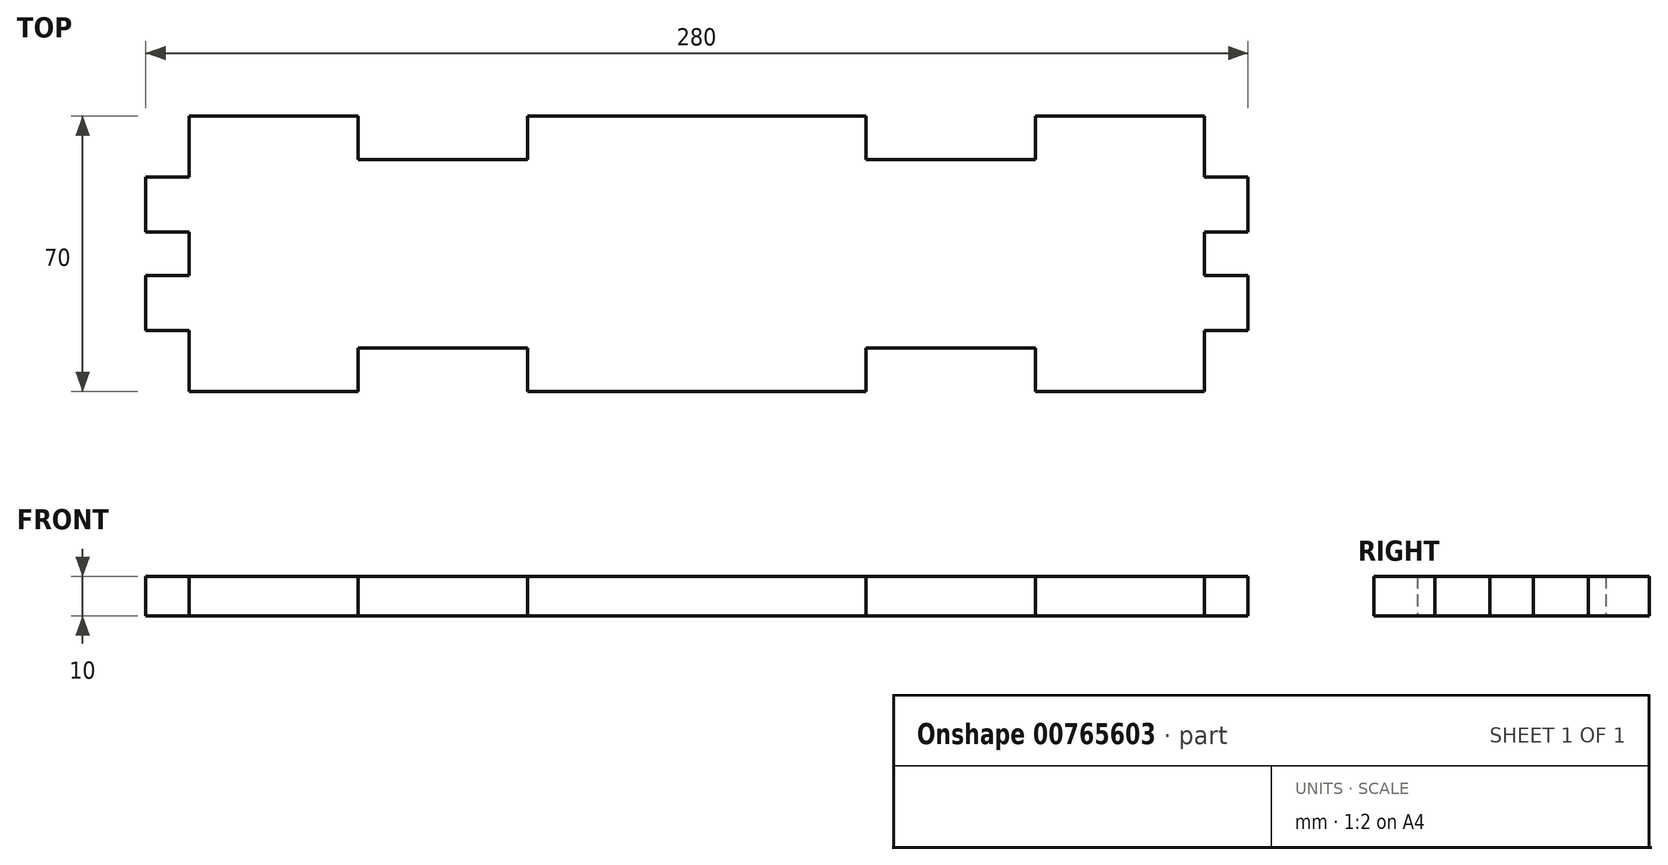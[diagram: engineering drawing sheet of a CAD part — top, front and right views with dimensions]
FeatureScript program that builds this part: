
annotation { "Feature Type Name" : "Feature", "Feature Type Description" : "" }
export const myFeature = defineFeature(function(context is Context, id is Id, definition is map)
    precondition{}
    {
        {
            var Q0;
            Q0=qCreatedBy(makeId("Top.planeOp"),FACE);
            var sketch = newSketch(context, id + "F0", { "sketchPlane" : qUnion([Q0])});
            skPoint(sketch, "E0.middle", {"position": v(0, 0) * mm});
            skLineSegment(sketch, "E1", {"start": v(129, 35) * mm, "end": v(129, 19.5) * mm});
            skLineSegment(sketch, "E2", {"start": v(129, 19.5) * mm, "end": v(140, 19.5) * mm});
            skLineSegment(sketch, "E3", {"start": v(140, 19.5) * mm, "end": v(140, 5.5) * mm});
            skLineSegment(sketch, "E4.MirrorCS", {"start": v(129, -35) * mm, "end": v(129, -19.5) * mm});
            skLineSegment(sketch, "E5.MirrorCS", {"start": v(129, -19.5) * mm, "end": v(140, -19.5) * mm});
            skLineSegment(sketch, "E6.MirrorCS", {"start": v(140, -19.5) * mm, "end": v(140, -5.5) * mm});
            skLineSegment(sketch, "E7", {"start": v(140, -5.5) * mm, "end": v(129, -5.5) * mm});
            skLineSegment(sketch, "E8", {"start": v(129, -5.5) * mm, "end": v(129, 5.5) * mm});
            skLineSegment(sketch, "E9", {"start": v(129, 5.5) * mm, "end": v(140, 5.5) * mm});
            skLineSegment(sketch, "E10.MirrorCS", {"start": v(-129, 35) * mm, "end": v(-129, 19.5) * mm});
            skLineSegment(sketch, "E11.MirrorCS", {"start": v(-129, 19.5) * mm, "end": v(-140, 19.5) * mm});
            skLineSegment(sketch, "E12.MirrorCS", {"start": v(-140, 19.5) * mm, "end": v(-140, 5.5) * mm});
            skLineSegment(sketch, "E13.MirrorCS", {"start": v(-129, 5.5) * mm, "end": v(-140, 5.5) * mm});
            skLineSegment(sketch, "E14.MirrorCS", {"start": v(-129, -5.5) * mm, "end": v(-129, 5.5) * mm});
            skLineSegment(sketch, "E15.MirrorCS", {"start": v(-140, -5.5) * mm, "end": v(-129, -5.5) * mm});
            skLineSegment(sketch, "E16.MirrorCS", {"start": v(-140, -19.5) * mm, "end": v(-140, -5.5) * mm});
            skLineSegment(sketch, "E17.MirrorCS", {"start": v(-129, -19.5) * mm, "end": v(-140, -19.5) * mm});
            skLineSegment(sketch, "E18.MirrorCS", {"start": v(-129, -35) * mm, "end": v(-129, -19.5) * mm});
            skLineSegment(sketch, "E19", {"start": v(-129, 35) * mm, "end": v(-86, 35) * mm});
            skLineSegment(sketch, "E20", {"start": v(-86, 35) * mm, "end": v(-86, 24) * mm});
            skLineSegment(sketch, "E21", {"start": v(-86, 24) * mm, "end": v(-43, 24) * mm});
            skLineSegment(sketch, "E22", {"start": v(-43, 24) * mm, "end": v(-43, 35) * mm});
            skLineSegment(sketch, "E23.MirrorCS", {"start": v(86, 35) * mm, "end": v(86, 24) * mm});
            skLineSegment(sketch, "E24.MirrorCS", {"start": v(86, 24) * mm, "end": v(43, 24) * mm});
            skLineSegment(sketch, "E25", {"start": v(86, 35) * mm, "end": v(129, 35) * mm});
            skLineSegment(sketch, "E26", {"start": v(43, 24) * mm, "end": v(43, 35) * mm});
            skLineSegment(sketch, "E27", {"start": v(-43, 35) * mm, "end": v(43, 35) * mm});
            skLineSegment(sketch, "E28.MirrorCS", {"start": v(-129, -35) * mm, "end": v(-86, -35) * mm});
            skLineSegment(sketch, "E29.MirrorCS", {"start": v(-86, -35) * mm, "end": v(-86, -24) * mm});
            skLineSegment(sketch, "E30.MirrorCS", {"start": v(-86, -24) * mm, "end": v(-43, -24) * mm});
            skLineSegment(sketch, "E31.MirrorCS", {"start": v(-43, -24) * mm, "end": v(-43, -35) * mm});
            skLineSegment(sketch, "E32.MirrorCS", {"start": v(-43, -35) * mm, "end": v(43, -35) * mm});
            skLineSegment(sketch, "E33.MirrorCS", {"start": v(43, -24) * mm, "end": v(43, -35) * mm});
            skLineSegment(sketch, "E34.MirrorCS", {"start": v(86, -24) * mm, "end": v(43, -24) * mm});
            skLineSegment(sketch, "E35.MirrorCS", {"start": v(86, -35) * mm, "end": v(86, -24) * mm});
            skLineSegment(sketch, "E36.MirrorCS", {"start": v(86, -35) * mm, "end": v(129, -35) * mm});
            skSolve(sketch);
        }
        {
            var Q0;
            Q0=makeQuery(id+"F0.imprint","IMPRINT",FACE,{"disambiguationData":[TD([[makeQuery(id+"F0.imprint","IMPRINT",EDGE,{"derivedFrom":sQuery(id+"F0.wireOp",EDGE,"E1")}),-1.0]])]});
            extrude(context, id + "F1", {"entities" : qUnion([Q0]), "depth" : 10 * mm, "offsetDistance" : 25 * mm});
        }
    });
